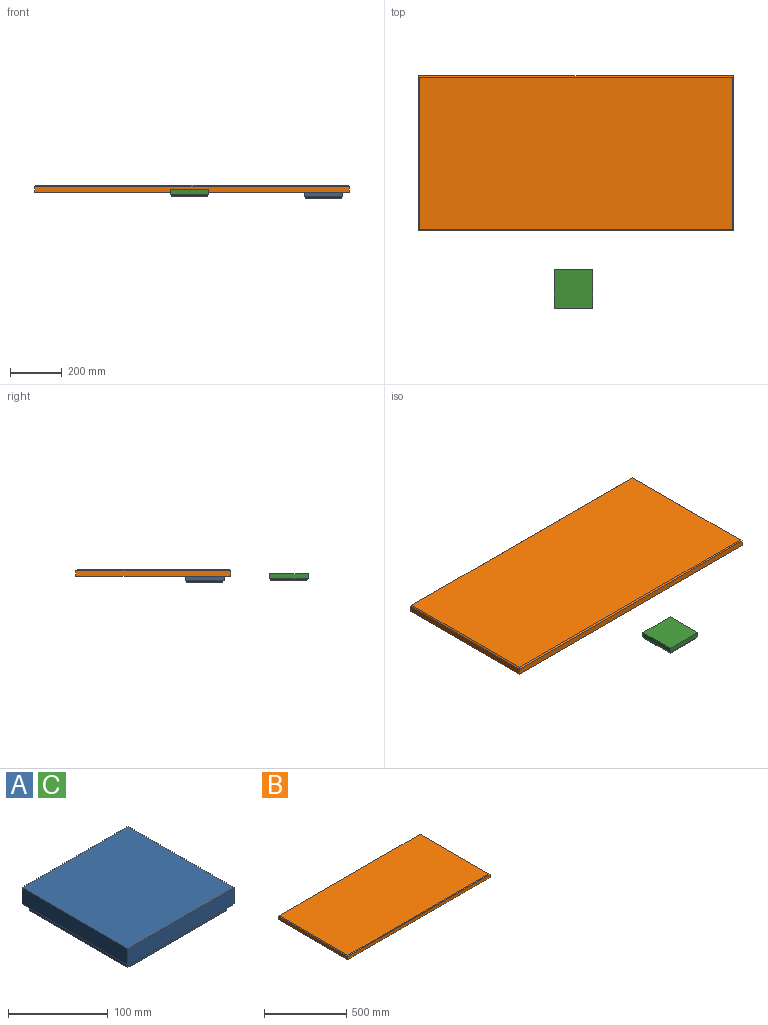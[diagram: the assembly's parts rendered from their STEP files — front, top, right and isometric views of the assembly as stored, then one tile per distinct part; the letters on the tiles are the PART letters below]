
ASSEMBLY  parts=3 mates=1
PART A: 19 faces, bbox 150x150x28 mm
  f0: plane 150x20mm, normal (1,0,0), area 3000mm2, adj f1,f3,f4,f5
  f1: plane 150x20mm, normal (0,1,0), area 3000mm2, adj f0,f2,f4,f6
  f2: plane 150x20mm, normal (-1,0,0), area 3000mm2, adj f1,f3,f4,f8
  f3: plane 150x20mm, normal (0,-1,0), area 3000mm2, adj f0,f2,f4,f7
  f4: plane 150x150mm, normal (0,0,1), area 22500mm2, adj f0,f1,f2,f3
  f5: plane 150x5mm, normal (0.71,0,-0.71), area 1025.3mm2, adj f0,f6,f7,f10
  f6: plane 150x5mm, normal (0,0.71,-0.71), area 1025.3mm2, adj f1,f5,f8,f9
  f7: plane 150x5mm, normal (0,-0.71,-0.71), area 1025.3mm2, adj f3,f5,f8,f11
  f8: plane 150x5mm, normal (-0.71,0,-0.71), area 1025.3mm2, adj f2,f6,f7,f16
  f9: plane 140x3mm, normal (0,1,0), area 420mm2, adj f6,f10,f16,f17
  f10: plane 140x3mm, normal (1,0,0), area 420mm2, adj f5,f9,f11,f17
  f11: plane 140x3mm, normal (0,-1,0), area 420mm2, adj f7,f10,f16,f17
  f12: plane 100x3mm, normal (-1,0,0), area 300mm2, adj f13,f15,f17,f18
  f13: plane 100x3mm, normal (0,-1,0), area 300mm2, adj f12,f14,f17,f18
  f14: plane 100x3mm, normal (1,0,0), area 300mm2, adj f13,f15,f17,f18
  f15: plane 100x3mm, normal (0,1,0), area 300mm2, adj f12,f14,f17,f18
  f16: plane 140x3mm, normal (-1,0,0), area 420mm2, adj f8,f9,f11,f17
  f17: plane 140x140mm, normal (0,0,-1), area 9600mm2, adj f9,f10,f11,f12,f13,f14,f15,f16
  f18: plane 100x100mm, normal (0,0,-1), area 10000mm2, adj f12,f13,f14,f15
PART B: 50 faces, bbox 1220x600x28 mm
  f0: plane 600x23mm, normal (1,0,0), area 13800mm2, adj f1,f3,f37,f49
  f1: plane 1220x23mm, normal (0,1,0), area 28060mm2, adj f0,f2,f37,f47
  f2: plane 600x23mm, normal (-1,0,0), area 13800mm2, adj f1,f3,f37,f46
  f3: plane 1220x23mm, normal (0,-1,0), area 28060mm2, adj f0,f2,f37,f48
  f4: plane 1210x590mm, normal (0,0,1), area 713900mm2, adj f46,f47,f48,f49
  f5: plane 100x3mm, normal (1,0,0), area 300mm2, adj f6,f29,f37,f44
  f6: plane 100x3mm, normal (0,1,0), area 300mm2, adj f5,f7,f37,f44
  f7: plane 100x3mm, normal (-1,0,0), area 300mm2, adj f6,f29,f37,f44
  f8: plane 100x3mm, normal (1,0,0), area 300mm2, adj f9,f30,f37,f43
  f9: plane 100x3mm, normal (0,1,0), area 300mm2, adj f8,f10,f37,f43
  f10: plane 100x3mm, normal (-1,0,0), area 300mm2, adj f9,f30,f37,f43
  f11: plane 100x3mm, normal (1,0,0), area 300mm2, adj f12,f31,f37,f42
  f12: plane 100x3mm, normal (0,1,0), area 300mm2, adj f11,f13,f37,f42
  f13: plane 100x3mm, normal (-1,0,0), area 300mm2, adj f12,f31,f37,f42
  f14: plane 100x3mm, normal (1,0,0), area 300mm2, adj f15,f32,f37,f41
  f15: plane 100x3mm, normal (0,1,0), area 300mm2, adj f14,f16,f37,f41
  f16: plane 100x3mm, normal (-1,0,0), area 300mm2, adj f15,f32,f37,f41
  f17: plane 150x3mm, normal (1,0,0), area 450mm2, adj f18,f33,f37,f40
  f18: plane 150x3mm, normal (0,1,0), area 450mm2, adj f17,f19,f37,f40
  f19: plane 150x3mm, normal (-1,0,0), area 450mm2, adj f18,f33,f37,f40
  f20: plane 150x3mm, normal (1,0,0), area 450mm2, adj f21,f34,f37,f39
  f21: plane 150x3mm, normal (0,1,0), area 450mm2, adj f20,f22,f37,f39
  f22: plane 150x3mm, normal (-1,0,0), area 450mm2, adj f21,f34,f37,f39
  f23: plane 150x3mm, normal (1,0,0), area 450mm2, adj f24,f35,f37,f38
  f24: plane 150x3mm, normal (0,1,0), area 450mm2, adj f23,f25,f37,f38
  f25: plane 150x3mm, normal (-1,0,0), area 450mm2, adj f24,f35,f37,f38
  f26: plane 150x3mm, normal (1,0,0), area 450mm2, adj f27,f36,f37,f45
  f27: plane 150x3mm, normal (0,1,0), area 450mm2, adj f26,f28,f37,f45
  f28: plane 150x3mm, normal (-1,0,0), area 450mm2, adj f27,f36,f37,f45
  f29: plane 100x3mm, normal (0,-1,0), area 300mm2, adj f5,f7,f37,f44
  f30: plane 100x3mm, normal (0,-1,0), area 300mm2, adj f8,f10,f37,f43
  f31: plane 100x3mm, normal (0,-1,0), area 300mm2, adj f11,f13,f37,f42
  f32: plane 100x3mm, normal (0,-1,0), area 300mm2, adj f14,f16,f37,f41
  f33: plane 150x3mm, normal (0,-1,0), area 450mm2, adj f17,f19,f37,f40
  f34: plane 150x3mm, normal (0,-1,0), area 450mm2, adj f20,f22,f37,f39
  f35: plane 150x3mm, normal (0,-1,0), area 450mm2, adj f23,f25,f37,f38
  f36: plane 150x3mm, normal (0,-1,0), area 450mm2, adj f26,f28,f37,f45
  f37: plane 1220x600mm, normal (0,0,-1), area 602000mm2, adj f0,f1,f2,f3,f5,f6,f7,f8
  f38: plane 150x150mm, normal (0,0,-1), area 22500mm2, adj f23,f24,f25,f35
  f39: plane 150x150mm, normal (0,0,-1), area 22500mm2, adj f20,f21,f22,f34
  f40: plane 150x150mm, normal (0,0,-1), area 22500mm2, adj f17,f18,f19,f33
  f41: plane 100x100mm, normal (0,0,-1), area 10000mm2, adj f14,f15,f16,f32
  f42: plane 100x100mm, normal (0,0,-1), area 10000mm2, adj f11,f12,f13,f31
  f43: plane 100x100mm, normal (0,0,-1), area 10000mm2, adj f8,f9,f10,f30
  f44: plane 100x100mm, normal (0,0,-1), area 10000mm2, adj f5,f6,f7,f29
  f45: plane 150x150mm, normal (0,0,-1), area 22500mm2, adj f26,f27,f28,f36
  f46: plane 600x5mm, normal (-0.71,0,0.71), area 4207.3mm2, adj f2,f4,f47,f48
  f47: plane 1220x5mm, normal (0,0.71,0.71), area 8591.3mm2, adj f1,f4,f46,f49
  f48: plane 1220x5mm, normal (0,-0.71,0.71), area 8591.3mm2, adj f3,f4,f46,f49
  f49: plane 600x5mm, normal (0.71,0,0.71), area 4207.3mm2, adj f0,f4,f47,f48
PART C: same geometry as A
PLACE A rot(axis=(0,0,1),180deg) t=(519.41,326.18,-7.49)mm
PLACE B t=(9.41,526.18,17.51)mm
PLACE C at identity
MATE revolute A.f4 <-> B.f39  axis (0,0,1) through (519.41,326.18,17.51)mm
